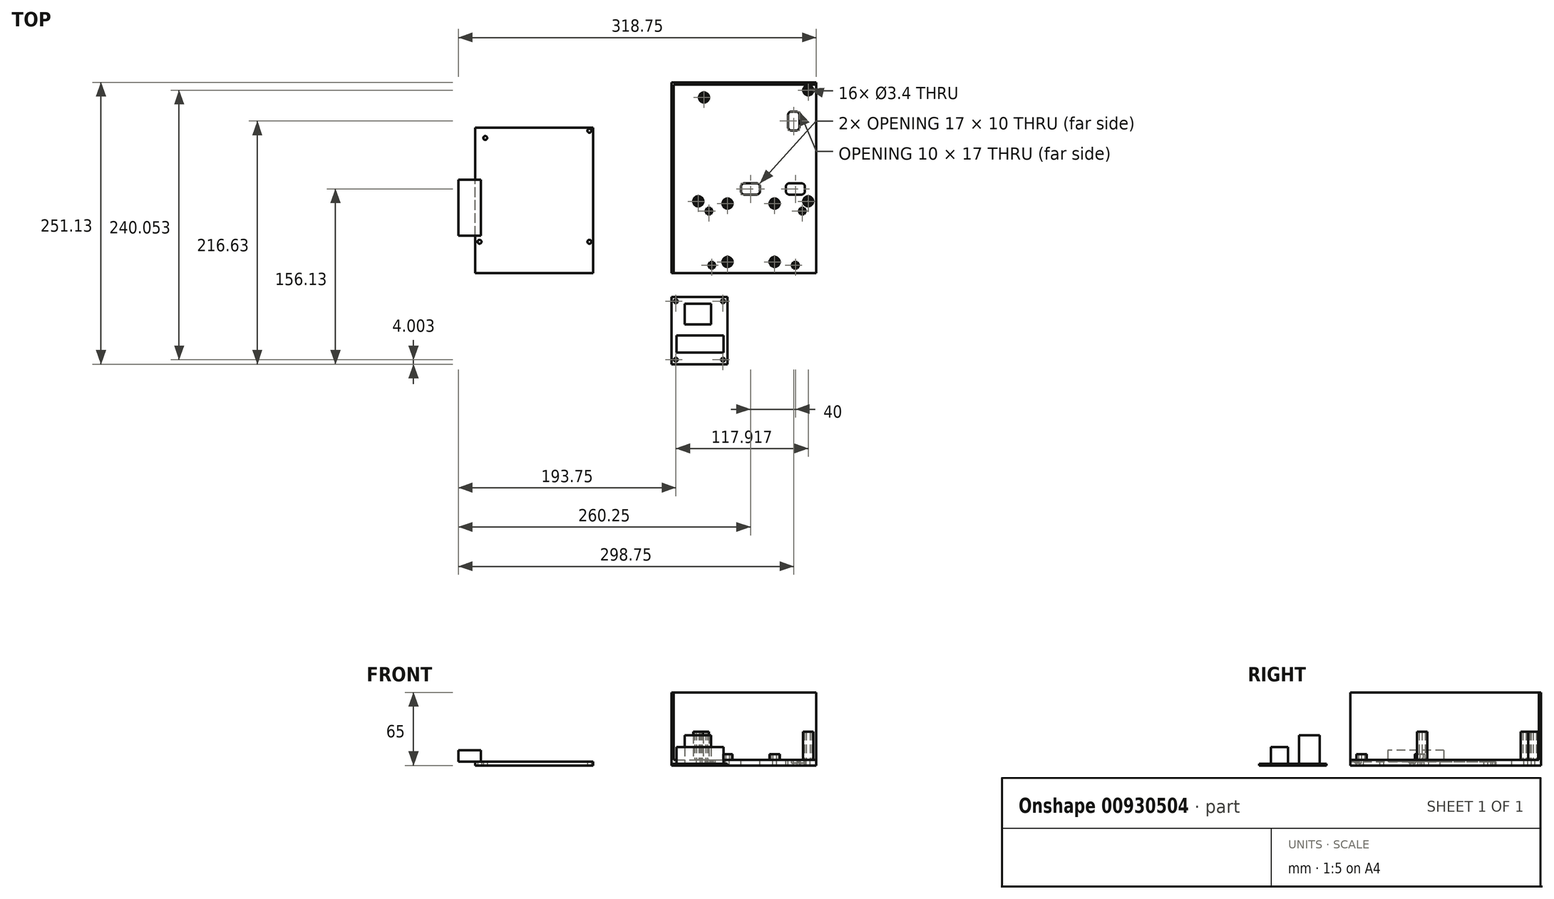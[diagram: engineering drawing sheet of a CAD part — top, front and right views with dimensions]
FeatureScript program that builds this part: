
annotation { "Feature Type Name" : "Feature", "Feature Type Description" : "" }
export const myFeature = defineFeature(function(context is Context, id is Id, definition is map)
    precondition{}
    {
        {
            assignVariable(context, id + "F0", {"variableType" : VariableType.LENGTH, "name" : "M3HoleDiameter", "lengthValue" : 3.4 * mm});
        }
        {
            assignVariable(context, id + "F1", {"variableType" : VariableType.LENGTH, "name" : "M3HexNutDepth", "lengthValue" : 2.8 * mm});
        }
        {
            var Q0;
            Q0=qCreatedBy(makeId("Top.planeOp"),FACE);
            var sketch = newSketch(context, id + "F2", { "sketchPlane" : qUnion([Q0])});
            skLineSegment(sketch, "E0.bottom", {"start": v(-174.75, 0) * mm, "end": v(-69.71, 0) * mm});
            skLineSegment(sketch, "E0.top", {"start": v(-174.75, 129.57) * mm, "end": v(-69.71, 129.57) * mm});
            skLineSegment(sketch, "E0.left", {"start": v(-174.75, 0) * mm, "end": v(-174.75, 129.57) * mm});
            skLineSegment(sketch, "E0.right", {"start": v(-69.71, 0) * mm, "end": v(-69.71, 129.57) * mm});
            skPoint(sketch, "E1", {"position": v(-170.94, 27.96) * mm});
            skPoint(sketch, "E2", {"position": v(-73.03, 27.96) * mm});
            skPoint(sketch, "E3", {"position": v(-73.03, 126.88) * mm});
            skPoint(sketch, "E4", {"position": v(-165.86, 120.41) * mm});
            skCircle(sketch, "E5", {"center": v(-165.86, 120.41) * mm, "radius": 1.75 * mm});
            skCircle(sketch, "E6", {"center": v(-73.03, 126.88) * mm, "radius": 1.75 * mm});
            skCircle(sketch, "E7", {"center": v(-170.94, 27.96) * mm, "radius": 1.75 * mm});
            skCircle(sketch, "E8", {"center": v(-73.03, 27.96) * mm, "radius": 1.75 * mm});
            skSolve(sketch);
        }
        {
            var Q0;
            Q0 = qSketchRegion(id + "F2", true);
            extrude(context, id + "F3", {"entities" : qUnion([Q0]), "depth" : 3.5 * mm, "offsetDistance" : 25 * mm});
        }
        {
            var Q0;
            Q0=makeQuery(id+"F3.opExtrude","CAP_FACE",FACE,{"disambiguationData":[OSD([sQuery(id+"F2.wireOp",EDGE,"E0.bottom"),sQuery(id+"F2.wireOp",EDGE,"E0.top"),sQuery(id+"F2.wireOp",EDGE,"E0.left"),sQuery(id+"F2.wireOp",EDGE,"E0.right"),sQuery(id+"F2.wireOp",EDGE,"E5"),sQuery(id+"F2.wireOp",EDGE,"E6"),sQuery(id+"F2.wireOp",EDGE,"E7"),sQuery(id+"F2.wireOp",EDGE,"E8")])],"isStart":false});
            var sketch = newSketch(context, id + "F4", { "sketchPlane" : qUnion([Q0])});
            skLineSegment(sketch, "E9.bottom", {"start": v(-174.75, 33.29) * mm, "end": v(-189.75, 33.29) * mm});
            skLineSegment(sketch, "E9.top", {"start": v(-174.75, 83.29) * mm, "end": v(-189.75, 83.29) * mm});
            skLineSegment(sketch, "E9.left", {"start": v(-174.75, 33.29) * mm, "end": v(-174.75, 83.29) * mm});
            skLineSegment(sketch, "E9.right", {"start": v(-189.75, 33.29) * mm, "end": v(-189.75, 83.29) * mm});
            skLineSegment(sketch, "E10.bottom", {"start": v(-174.75, 83.29) * mm, "end": v(-169.75, 83.29) * mm});
            skLineSegment(sketch, "E10.top", {"start": v(-174.75, 33.29) * mm, "end": v(-169.75, 33.29) * mm});
            skLineSegment(sketch, "E10.left", {"start": v(-174.75, 83.29) * mm, "end": v(-174.75, 33.29) * mm});
            skLineSegment(sketch, "E10.right", {"start": v(-169.75, 83.29) * mm, "end": v(-169.75, 33.29) * mm});
            skSolve(sketch);
        }
        {
            var Q0;
            Q0 = qSketchRegion(id + "F4", true);
            extrude(context, id + "F5", {"entities" : qUnion([Q0]), "operationType" : NewBodyOperationType.ADD, "depth" : 10 * mm, "offsetDistance" : 25 * mm});
        }
        {
            var Q0;
            Q0=qCreatedBy(makeId("Top.planeOp"),FACE);
            var sketch = newSketch(context, id + "F6", { "sketchPlane" : qUnion([Q0])});
            skLineSegment(sketch, "E11.bottom", {"start": v(0, -81.13) * mm, "end": v(50, -81.13) * mm});
            skLineSegment(sketch, "E11.top", {"start": v(0, -21.13) * mm, "end": v(50, -21.13) * mm});
            skLineSegment(sketch, "E11.left", {"start": v(0, -81.13) * mm, "end": v(0, -21.13) * mm});
            skLineSegment(sketch, "E11.right", {"start": v(50, -81.13) * mm, "end": v(50, -21.13) * mm});
            skPoint(sketch, "E12", {"position": v(4, -25.13) * mm});
            skPoint(sketch, "E13", {"position": v(46, -25.13) * mm});
            skPoint(sketch, "E14", {"position": v(4, -77.13) * mm});
            skPoint(sketch, "E15", {"position": v(46, -77.13) * mm});
            skCircle(sketch, "E16", {"center": v(4, -25.13) * mm, "radius": 1.7 * mm});
            skCircle(sketch, "E17", {"center": v(46, -25.13) * mm, "radius": 1.7 * mm});
            skCircle(sketch, "E18", {"center": v(4, -77.13) * mm, "radius": 1.7 * mm});
            skCircle(sketch, "E19", {"center": v(46, -77.13) * mm, "radius": 1.7 * mm});
            skSolve(sketch);
        }
        {
            var Q0;
            Q0 = qSketchRegion(id + "F6", true);
            extrude(context, id + "F7", {"entities" : qUnion([Q0]), "depth" : 1.5 * mm, "offsetDistance" : 25 * mm});
        }
        {
            var Q0;
            Q0=makeQuery(id+"F7.opExtrude","CAP_FACE",FACE,{"disambiguationData":[OSD([sQuery(id+"F6.wireOp",EDGE,"E11.bottom"),sQuery(id+"F6.wireOp",EDGE,"E11.top"),sQuery(id+"F6.wireOp",EDGE,"E11.left"),sQuery(id+"F6.wireOp",EDGE,"E11.right"),sQuery(id+"F6.wireOp",EDGE,"E16"),sQuery(id+"F6.wireOp",EDGE,"E17"),sQuery(id+"F6.wireOp",EDGE,"E18"),sQuery(id+"F6.wireOp",EDGE,"E19")])],"isStart":false});
            var sketch = newSketch(context, id + "F8", { "sketchPlane" : qUnion([Q0])});
            skLineSegment(sketch, "E20.bottom", {"start": v(4.5, -70.63) * mm, "end": v(46.5, -70.63) * mm});
            skLineSegment(sketch, "E20.top", {"start": v(4.5, -55.63) * mm, "end": v(46.5, -55.63) * mm});
            skLineSegment(sketch, "E20.left", {"start": v(4.5, -70.63) * mm, "end": v(4.5, -55.63) * mm});
            skLineSegment(sketch, "E20.right", {"start": v(46.5, -70.63) * mm, "end": v(46.5, -55.63) * mm});
            skSolve(sketch);
        }
        {
            var Q0;
            Q0 = qSketchRegion(id + "F8", true);
            extrude(context, id + "F9", {"entities" : qUnion([Q0]), "operationType" : NewBodyOperationType.ADD, "depth" : 15 * mm, "offsetDistance" : 25 * mm});
        }
        {
            var Q0;
            Q0=makeQuery(id+"F7.opExtrude","CAP_FACE",FACE,{"disambiguationData":[OSD([sQuery(id+"F6.wireOp",EDGE,"E11.bottom"),sQuery(id+"F6.wireOp",EDGE,"E11.top"),sQuery(id+"F6.wireOp",EDGE,"E11.left"),sQuery(id+"F6.wireOp",EDGE,"E11.right"),sQuery(id+"F6.wireOp",EDGE,"E16"),sQuery(id+"F6.wireOp",EDGE,"E17"),sQuery(id+"F6.wireOp",EDGE,"E18"),sQuery(id+"F6.wireOp",EDGE,"E19")])],"isStart":false});
            var sketch = newSketch(context, id + "F10", { "sketchPlane" : qUnion([Q0])});
            skLineSegment(sketch, "E21.bottom", {"start": v(11.75, -27.13) * mm, "end": v(35.25, -27.13) * mm});
            skLineSegment(sketch, "E21.top", {"start": v(11.75, -45.63) * mm, "end": v(35.25, -45.63) * mm});
            skLineSegment(sketch, "E21.left", {"start": v(11.75, -27.13) * mm, "end": v(11.75, -45.63) * mm});
            skLineSegment(sketch, "E21.right", {"start": v(35.25, -27.13) * mm, "end": v(35.25, -45.63) * mm});
            skSolve(sketch);
        }
        {
            var Q0;
            Q0 = qSketchRegion(id + "F10", true);
            extrude(context, id + "F11", {"entities" : qUnion([Q0]), "operationType" : NewBodyOperationType.ADD, "depth" : 25.5 * mm, "offsetDistance" : 25 * mm});
        }
        {
            var Q0;
            Q0=qCreatedBy(makeId("Top.planeOp"),FACE);
            var sketch = newSketch(context, id + "F12", { "sketchPlane" : qUnion([Q0])});
            skLineSegment(sketch, "E22.bottom", {"start": v(0, 0) * mm, "end": v(129, 0) * mm});
            skLineSegment(sketch, "E22.top", {"start": v(0, 170) * mm, "end": v(129, 170) * mm});
            skLineSegment(sketch, "E22.left", {"start": v(0, 0) * mm, "end": v(0, 170) * mm});
            skLineSegment(sketch, "E22.right", {"start": v(129, 0) * mm, "end": v(129, 170) * mm});
            skSolve(sketch);
        }
        {
            var Q0;
            Q0 = qSketchRegion(id + "F12", true);
            extrude(context, id + "F13", {"entities" : qUnion([Q0]), "depth" : 5 * mm, "offsetDistance" : 25 * mm});
        }
        {
            var Q0;
            Q0=makeQuery(id+"F13.opExtrude","CAP_FACE",FACE,{"disambiguationData":[OSD([sQuery(id+"F12.wireOp",EDGE,"E22.bottom"),sQuery(id+"F12.wireOp",EDGE,"E22.top"),sQuery(id+"F12.wireOp",EDGE,"E22.left"),sQuery(id+"F12.wireOp",EDGE,"E22.right"),sQuery(id+"F12.wireOp",EDGE,"ENlJJPwH-t7wi-Tg4m-EIBb-eTt2GZQg3k3P.top"),sQuery(id+"F12.wireOp",EDGE,"ENlJJPwH-t7wi-Tg4m-EIBb-eTt2GZQg3k3P.left"),sQuery(id+"F12.wireOp",EDGE,"ENlJJPwH-t7wi-Tg4m-EIBb-eTt2GZQg3k3P.right"),sQuery(id+"F12.wireOp",EDGE,"590sdj5N-QSTJ-qvK5-s69I-Y719Xk4BLkaZ.top"),sQuery(id+"F12.wireOp",EDGE,"590sdj5N-QSTJ-qvK5-s69I-Y719Xk4BLkaZ.left"),sQuery(id+"F12.wireOp",EDGE,"590sdj5N-QSTJ-qvK5-s69I-Y719Xk4BLkaZ.right"),sQuery(id+"F12.wireOp",EDGE,"boF4sXyi-6WZN-pan6-Kfs4-asuBxe9Vqafz.top"),sQuery(id+"F12.wireOp",EDGE,"boF4sXyi-6WZN-pan6-Kfs4-asuBxe9Vqafz.left"),sQuery(id+"F12.wireOp",EDGE,"boF4sXyi-6WZN-pan6-Kfs4-asuBxe9Vqafz.right"),sQuery(id+"F12.wireOp",EDGE,"VC2s6hMx-ooNF-aeXA-kSyT-K1uUBSIoU8fE.top"),sQuery(id+"F12.wireOp",EDGE,"VC2s6hMx-ooNF-aeXA-kSyT-K1uUBSIoU8fE.left"),sQuery(id+"F12.wireOp",EDGE,"VC2s6hMx-ooNF-aeXA-kSyT-K1uUBSIoU8fE.right")])],"isStart":false});
            var sketch = newSketch(context, id + "F14", { "sketchPlane" : qUnion([Q0])});
            skPoint(sketch, "E23", {"position": v(36, 7) * mm});
            skPoint(sketch, "E24", {"position": v(110.5, 7) * mm});
            skPoint(sketch, "E25", {"position": v(33.5, 55.2) * mm});
            skPoint(sketch, "E26", {"position": v(116.7, 55.2) * mm});
            skCircle(sketch, "E27.cCircle", {"center": v(33.5, 55.2) * mm, "radius": 2.8 * mm, "construction": true});
            skLineSegment(sketch, "E27.0", {"start": v(31.88, 58) * mm, "end": v(35.12, 58) * mm});
            skLineSegment(sketch, "E27.1", {"start": v(35.12, 58) * mm, "end": v(36.73, 55.2) * mm});
            skLineSegment(sketch, "E27.2", {"start": v(36.73, 55.2) * mm, "end": v(35.12, 52.4) * mm});
            skLineSegment(sketch, "E27.3", {"start": v(35.12, 52.4) * mm, "end": v(31.88, 52.4) * mm});
            skLineSegment(sketch, "E27.4", {"start": v(31.88, 52.4) * mm, "end": v(30.27, 55.2) * mm});
            skLineSegment(sketch, "E27.5", {"start": v(30.27, 55.2) * mm, "end": v(31.88, 58) * mm});
            skPoint(sketch, "E27.0.midPoint", {"position": v(33.5, 58) * mm});
            skCircle(sketch, "E28.cCircle", {"center": v(116.7, 55.2) * mm, "radius": 2.8 * mm, "construction": true});
            skLineSegment(sketch, "E28.0", {"start": v(115.08, 58) * mm, "end": v(118.32, 58) * mm});
            skLineSegment(sketch, "E28.1", {"start": v(118.32, 58) * mm, "end": v(119.93, 55.2) * mm});
            skLineSegment(sketch, "E28.2", {"start": v(119.93, 55.2) * mm, "end": v(118.32, 52.4) * mm});
            skLineSegment(sketch, "E28.3", {"start": v(118.32, 52.4) * mm, "end": v(115.08, 52.4) * mm});
            skLineSegment(sketch, "E28.4", {"start": v(115.08, 52.4) * mm, "end": v(113.47, 55.2) * mm});
            skLineSegment(sketch, "E28.5", {"start": v(113.47, 55.2) * mm, "end": v(115.08, 58) * mm});
            skPoint(sketch, "E28.0.midPoint", {"position": v(116.7, 58) * mm});
            skCircle(sketch, "E29.cCircle", {"center": v(110.5, 7) * mm, "radius": 2.8 * mm, "construction": true});
            skLineSegment(sketch, "E29.0", {"start": v(108.88, 9.8) * mm, "end": v(112.12, 9.8) * mm});
            skLineSegment(sketch, "E29.1", {"start": v(112.12, 9.8) * mm, "end": v(113.73, 7) * mm});
            skLineSegment(sketch, "E29.2", {"start": v(113.73, 7) * mm, "end": v(112.12, 4.2) * mm});
            skLineSegment(sketch, "E29.3", {"start": v(112.12, 4.2) * mm, "end": v(108.88, 4.2) * mm});
            skLineSegment(sketch, "E29.4", {"start": v(108.88, 4.2) * mm, "end": v(107.27, 7) * mm});
            skLineSegment(sketch, "E29.5", {"start": v(107.27, 7) * mm, "end": v(108.88, 9.8) * mm});
            skPoint(sketch, "E29.0.midPoint", {"position": v(110.5, 9.8) * mm});
            skCircle(sketch, "E30.cCircle", {"center": v(36, 7) * mm, "radius": 2.8 * mm, "construction": true});
            skLineSegment(sketch, "E30.0", {"start": v(34.38, 9.8) * mm, "end": v(37.62, 9.8) * mm});
            skLineSegment(sketch, "E30.1", {"start": v(37.62, 9.8) * mm, "end": v(39.23, 7) * mm});
            skLineSegment(sketch, "E30.2", {"start": v(39.23, 7) * mm, "end": v(37.62, 4.2) * mm});
            skLineSegment(sketch, "E30.3", {"start": v(37.62, 4.2) * mm, "end": v(34.38, 4.2) * mm});
            skLineSegment(sketch, "E30.4", {"start": v(34.38, 4.2) * mm, "end": v(32.77, 7) * mm});
            skLineSegment(sketch, "E30.5", {"start": v(32.77, 7) * mm, "end": v(34.38, 9.8) * mm});
            skPoint(sketch, "E30.0.midPoint", {"position": v(36, 9.8) * mm});
            skSolve(sketch);
        }
        {
            var Q0;
            Q0=sQuery(id+"F14.wireOp",VERTEX,"E25");
            var Q1;
            Q1=sQuery(id+"F14.wireOp",VERTEX,"E28.cCircle.center");
            var Q2;
            Q2=sQuery(id+"F14.wireOp",VERTEX,"E29.cCircle.center");
            var Q3;
            Q3=sQuery(id+"F14.wireOp",VERTEX,"E30.cCircle.center");
            var Q4;
            Q4=sQuery(id+"F14.wireOp",VERTEX,"66780121-3f7c-4df2-9e8e-298b6627a8a1.cCircle.center");
            var Q5;
            Q5=sQuery(id+"F14.wireOp",VERTEX,"7a8d0383-0dc8-4305-b331-709482cf3036");
            var Q6;
            Q6=sQuery(id+"F14.wireOp",VERTEX,"6d33d0c3-34ed-4e35-861e-9c01af61f537");
            var Q7;
            Q7=sQuery(id+"F14.wireOp",VERTEX,"b813c6d9-d0bb-4b40-90eb-9f39a377eb20.cCircle.center");
            var Q8;
            Q8=sQuery(id+"F14.wireOp",VERTEX,"7464b1d7-4f39-41f7-8282-fd3c08e524e5");
            var Q9;
            Q9=sQuery(id+"F14.wireOp",VERTEX,"ce837585-52f0-452e-9ccc-18a1bac3b544");
            var Q10;
            Q10=makeQuery(id+"F13.opExtrude","SWEPT_BODY",BODY,{"disambiguationData":[OSD([sQuery(id+"F12.wireOp",EDGE,"E22.bottom"),sQuery(id+"F12.wireOp",EDGE,"E22.top"),sQuery(id+"F12.wireOp",EDGE,"E22.left"),sQuery(id+"F12.wireOp",EDGE,"E22.right"),sQuery(id+"F12.wireOp",EDGE,"ENlJJPwH-t7wi-Tg4m-EIBb-eTt2GZQg3k3P.top"),sQuery(id+"F12.wireOp",EDGE,"ENlJJPwH-t7wi-Tg4m-EIBb-eTt2GZQg3k3P.left"),sQuery(id+"F12.wireOp",EDGE,"ENlJJPwH-t7wi-Tg4m-EIBb-eTt2GZQg3k3P.right"),sQuery(id+"F12.wireOp",EDGE,"590sdj5N-QSTJ-qvK5-s69I-Y719Xk4BLkaZ.top"),sQuery(id+"F12.wireOp",EDGE,"590sdj5N-QSTJ-qvK5-s69I-Y719Xk4BLkaZ.left"),sQuery(id+"F12.wireOp",EDGE,"590sdj5N-QSTJ-qvK5-s69I-Y719Xk4BLkaZ.right"),sQuery(id+"F12.wireOp",EDGE,"boF4sXyi-6WZN-pan6-Kfs4-asuBxe9Vqafz.top"),sQuery(id+"F12.wireOp",EDGE,"boF4sXyi-6WZN-pan6-Kfs4-asuBxe9Vqafz.left"),sQuery(id+"F12.wireOp",EDGE,"boF4sXyi-6WZN-pan6-Kfs4-asuBxe9Vqafz.right"),sQuery(id+"F12.wireOp",EDGE,"VC2s6hMx-ooNF-aeXA-kSyT-K1uUBSIoU8fE.top"),sQuery(id+"F12.wireOp",EDGE,"VC2s6hMx-ooNF-aeXA-kSyT-K1uUBSIoU8fE.left"),sQuery(id+"F12.wireOp",EDGE,"VC2s6hMx-ooNF-aeXA-kSyT-K1uUBSIoU8fE.right")])]});
            hole(context, id + "F15", {"style" : HoleStyle.SIMPLE, "endStyle" : HoleEndStyle.THROUGH, "holeDiameter" : getVariable(context, 'M3HoleDiameter'), "majorDiameter" : 5 * mm, "isTappedThrough" : true, "tappedDepth" : 12 * mm, "tapClearance" : 3, "locations" : qUnion([Q0, Q1, Q2, Q3, Q4, Q5, Q6, Q7, Q8, Q9]), "scope" : qUnion([Q10])});
        }
        {
            var Q0;
            Q0 = qSketchRegion(id + "F14", true);
            extrude(context, id + "F16", {"entities" : qUnion([Q0]), "operationType" : NewBodyOperationType.REMOVE, "oppositeDirection" : true, "depth" : getVariable(context, 'M3HexNutDepth'), "offsetDistance" : 25 * mm});
        }
        {
            var Q0;
            {var subQ0=sQuery(id+"F12.wireOp",EDGE,"VC2s6hMx-ooNF-aeXA-kSyT-K1uUBSIoU8fE.right");var subQ1=sQuery(id+"F12.wireOp",EDGE,"VC2s6hMx-ooNF-aeXA-kSyT-K1uUBSIoU8fE.top");var subQ2=sQuery(id+"F12.wireOp",EDGE,"boF4sXyi-6WZN-pan6-Kfs4-asuBxe9Vqafz.left");var subQ3=sQuery(id+"F12.wireOp",EDGE,"ENlJJPwH-t7wi-Tg4m-EIBb-eTt2GZQg3k3P.left");var subQ4=sQuery(id+"F12.wireOp",EDGE,"E22.left");var subQ5=sQuery(id+"F12.wireOp",EDGE,"E22.top");var subQ6=sQuery(id+"F12.wireOp",EDGE,"VC2s6hMx-ooNF-aeXA-kSyT-K1uUBSIoU8fE.left");var subQ7=sQuery(id+"F12.wireOp",EDGE,"590sdj5N-QSTJ-qvK5-s69I-Y719Xk4BLkaZ.left");var subQ8=sQuery(id+"F12.wireOp",EDGE,"E22.right");var subQ9=sQuery(id+"F12.wireOp",EDGE,"E22.bottom");var subQ10=sQuery(id+"F12.wireOp",EDGE,"boF4sXyi-6WZN-pan6-Kfs4-asuBxe9Vqafz.right");var subQ11=sQuery(id+"F12.wireOp",EDGE,"ENlJJPwH-t7wi-Tg4m-EIBb-eTt2GZQg3k3P.top");var subQ12=sQuery(id+"F12.wireOp",EDGE,"ENlJJPwH-t7wi-Tg4m-EIBb-eTt2GZQg3k3P.right");var subQ13=sQuery(id+"F12.wireOp",EDGE,"590sdj5N-QSTJ-qvK5-s69I-Y719Xk4BLkaZ.top");var subQ14=sQuery(id+"F12.wireOp",EDGE,"590sdj5N-QSTJ-qvK5-s69I-Y719Xk4BLkaZ.right");var subQ15=sQuery(id+"F12.wireOp",EDGE,"boF4sXyi-6WZN-pan6-Kfs4-asuBxe9Vqafz.top");Q0=makeQuery(id+"FK80XC3gcnQsNLE_2.boolean.opBoolean","SPLIT",FACE,{"disambiguationData":[TD([makeQuery(id+"F13.opExtrude","SWEPT_FACE",FACE,{"disambiguationData":[OSD([subQ9])]})])],"derivedFrom":makeQuery(id+"F13.opExtrude","CAP_FACE",FACE,{"disambiguationData":[OSD([subQ9,subQ5,subQ4,subQ8,subQ11,subQ3,subQ12,subQ13,subQ7,subQ14,subQ15,subQ2,subQ10,subQ1,subQ6,subQ0])],"isStart":false})});}
            var sketch = newSketch(context, id + "F17", { "sketchPlane" : qUnion([Q0])});
            skPoint(sketch, "E31", {"position": v(24, 64) * mm});
            skPoint(sketch, "E32", {"position": v(121.92, 64) * mm});
            skPoint(sketch, "E33", {"position": v(29.08, 156.46) * mm});
            skPoint(sketch, "E34", {"position": v(121.92, 162.93) * mm});
            skCircle(sketch, "E35", {"center": v(29.08, 156.46) * mm, "radius": 1.7 * mm});
            skCircle(sketch, "E36", {"center": v(29.08, 156.46) * mm, "radius": 4.5 * mm});
            skCircle(sketch, "E37", {"center": v(121.92, 162.93) * mm, "radius": 1.7 * mm});
            skCircle(sketch, "E38", {"center": v(121.92, 162.93) * mm, "radius": 4.5 * mm});
            skCircle(sketch, "E39", {"center": v(24, 64) * mm, "radius": 1.7 * mm});
            skCircle(sketch, "E40", {"center": v(24, 64) * mm, "radius": 4.5 * mm});
            skCircle(sketch, "E41", {"center": v(121.92, 64) * mm, "radius": 1.7 * mm});
            skCircle(sketch, "E42", {"center": v(121.92, 64) * mm, "radius": 4.5 * mm});
            skCircle(sketch, "E43.cCircle", {"center": v(29.08, 156.46) * mm, "radius": 2.8 * mm, "construction": true});
            skLineSegment(sketch, "E43.0", {"start": v(27.46, 159.26) * mm, "end": v(30.7, 159.26) * mm});
            skLineSegment(sketch, "E43.1", {"start": v(30.7, 159.26) * mm, "end": v(32.31, 156.46) * mm});
            skLineSegment(sketch, "E43.2", {"start": v(32.31, 156.46) * mm, "end": v(30.7, 153.66) * mm});
            skLineSegment(sketch, "E43.3", {"start": v(30.7, 153.66) * mm, "end": v(27.46, 153.66) * mm});
            skLineSegment(sketch, "E43.4", {"start": v(27.46, 153.66) * mm, "end": v(25.85, 156.46) * mm});
            skLineSegment(sketch, "E43.5", {"start": v(25.85, 156.46) * mm, "end": v(27.46, 159.26) * mm});
            skPoint(sketch, "E43.0.midPoint", {"position": v(29.08, 159.26) * mm});
            skCircle(sketch, "E44.cCircle", {"center": v(121.92, 162.93) * mm, "radius": 2.8 * mm, "construction": true});
            skLineSegment(sketch, "E44.0", {"start": v(120.3, 165.73) * mm, "end": v(123.53, 165.73) * mm});
            skLineSegment(sketch, "E44.1", {"start": v(123.53, 165.73) * mm, "end": v(125.15, 162.93) * mm});
            skLineSegment(sketch, "E44.2", {"start": v(125.15, 162.93) * mm, "end": v(123.53, 160.13) * mm});
            skLineSegment(sketch, "E44.3", {"start": v(123.53, 160.13) * mm, "end": v(120.3, 160.13) * mm});
            skLineSegment(sketch, "E44.4", {"start": v(120.3, 160.13) * mm, "end": v(118.68, 162.93) * mm});
            skLineSegment(sketch, "E44.5", {"start": v(118.68, 162.93) * mm, "end": v(120.3, 165.73) * mm});
            skPoint(sketch, "E44.0.midPoint", {"position": v(121.92, 165.73) * mm});
            skCircle(sketch, "E45.cCircle", {"center": v(24, 64) * mm, "radius": 2.8 * mm, "construction": true});
            skLineSegment(sketch, "E45.0", {"start": v(22.38, 66.8) * mm, "end": v(25.62, 66.8) * mm});
            skLineSegment(sketch, "E45.1", {"start": v(25.62, 66.8) * mm, "end": v(27.23, 64) * mm});
            skLineSegment(sketch, "E45.2", {"start": v(27.23, 64) * mm, "end": v(25.62, 61.2) * mm});
            skLineSegment(sketch, "E45.3", {"start": v(25.62, 61.2) * mm, "end": v(22.38, 61.2) * mm});
            skLineSegment(sketch, "E45.4", {"start": v(22.38, 61.2) * mm, "end": v(20.77, 64) * mm});
            skLineSegment(sketch, "E45.5", {"start": v(20.77, 64) * mm, "end": v(22.38, 66.8) * mm});
            skPoint(sketch, "E45.0.midPoint", {"position": v(24, 66.8) * mm});
            skCircle(sketch, "E46.cCircle", {"center": v(121.92, 64) * mm, "radius": 2.8 * mm, "construction": true});
            skLineSegment(sketch, "E46.0", {"start": v(120.3, 66.8) * mm, "end": v(123.53, 66.8) * mm});
            skLineSegment(sketch, "E46.1", {"start": v(123.53, 66.8) * mm, "end": v(125.15, 64) * mm});
            skLineSegment(sketch, "E46.2", {"start": v(125.15, 64) * mm, "end": v(123.53, 61.2) * mm});
            skLineSegment(sketch, "E46.3", {"start": v(123.53, 61.2) * mm, "end": v(120.3, 61.2) * mm});
            skLineSegment(sketch, "E46.4", {"start": v(120.3, 61.2) * mm, "end": v(118.68, 64) * mm});
            skLineSegment(sketch, "E46.5", {"start": v(118.68, 64) * mm, "end": v(120.3, 66.8) * mm});
            skPoint(sketch, "E46.0.midPoint", {"position": v(121.92, 66.8) * mm});
            skSolve(sketch);
        }
        {
            var Q0;
            Q0=sQuery(id+"F17.wireOp",VERTEX,"E33");
            var Q1;
            Q1=sQuery(id+"F17.wireOp",VERTEX,"E34");
            var Q2;
            Q2=sQuery(id+"F17.wireOp",VERTEX,"E32");
            var Q3;
            Q3=sQuery(id+"F17.wireOp",VERTEX,"E39.center");
            var Q4;
            Q4=makeQuery(id+"F13.opExtrude","SWEPT_BODY",BODY,{"disambiguationData":[OSD([sQuery(id+"F12.wireOp",EDGE,"E22.bottom"),sQuery(id+"F12.wireOp",EDGE,"E22.top"),sQuery(id+"F12.wireOp",EDGE,"E22.left"),sQuery(id+"F12.wireOp",EDGE,"E22.right")])]});
            hole(context, id + "F18", {"style" : HoleStyle.SIMPLE, "endStyle" : HoleEndStyle.THROUGH, "holeDiameter" : getVariable(context, 'M3HoleDiameter'), "majorDiameter" : 5 * mm, "isTappedThrough" : true, "tappedDepth" : 12 * mm, "tapClearance" : 3, "locations" : qUnion([Q0, Q1, Q2, Q3]), "scope" : qUnion([Q4])});
        }
        {
            var Q0;
            Q0 = qSketchRegion(id + "F17", true);
            extrude(context, id + "F19", {"entities" : qUnion([Q0]), "operationType" : NewBodyOperationType.ADD, "depth" : 25 * mm, "offsetDistance" : 25 * mm});
        }
        {
            var Q0;
            Q0=makeQuery(id+"F17.imprint","IMPRINT",FACE,{"disambiguationData":[TD([[makeQuery(id+"F17.imprint","IMPRINT",EDGE,{"derivedFrom":sQuery(id+"F17.wireOp",EDGE,"E36")}),-1.0]])]});
            var sketch = newSketch(context, id + "F20", { "sketchPlane" : qUnion([Q0])});
            skLineSegment(sketch, "E47", {"start": v(0, 0) * mm, "end": v(0, 170) * mm});
            skLineSegment(sketch, "E48", {"start": v(0, 170) * mm, "end": v(129, 170) * mm});
            skLineSegment(sketch, "E49", {"start": v(129, 170) * mm, "end": v(129, 168) * mm});
            skLineSegment(sketch, "E50", {"start": v(129, 168) * mm, "end": v(2, 168) * mm});
            skLineSegment(sketch, "E51", {"start": v(2, 168) * mm, "end": v(2, 0) * mm});
            skLineSegment(sketch, "E52", {"start": v(2, 0) * mm, "end": v(0, 0) * mm});
            skSolve(sketch);
        }
        {
            var Q0;
            Q0 = qSketchRegion(id + "F20", true);
            extrude(context, id + "F21", {"entities" : qUnion([Q0]), "operationType" : NewBodyOperationType.ADD, "depth" : 60 * mm, "offsetDistance" : 25 * mm});
        }
        {
            var Q0;
            Q0=makeQuery(id+"F17.imprint","IMPRINT",FACE,{"disambiguationData":[TD([[makeQuery(id+"F17.imprint","IMPRINT",EDGE,{"derivedFrom":sQuery(id+"F17.wireOp",EDGE,"E36")}),-1.0]])]});
            var sketch = newSketch(context, id + "F22", { "sketchPlane" : qUnion([Q0])});
            skPoint(sketch, "E53", {"position": v(50, 10) * mm});
            skPoint(sketch, "E54", {"position": v(92, 10) * mm});
            skPoint(sketch, "E55", {"position": v(50, 62) * mm});
            skPoint(sketch, "E56", {"position": v(92, 62) * mm});
            skCircle(sketch, "E57", {"center": v(50, 10) * mm, "radius": 1.7 * mm});
            skCircle(sketch, "E58", {"center": v(50, 10) * mm, "radius": 4.5 * mm});
            skCircle(sketch, "E59", {"center": v(92, 10) * mm, "radius": 1.7 * mm});
            skCircle(sketch, "E60", {"center": v(92, 10) * mm, "radius": 4.5 * mm});
            skCircle(sketch, "E61", {"center": v(50, 62) * mm, "radius": 1.7 * mm});
            skCircle(sketch, "E62", {"center": v(50, 62) * mm, "radius": 4.5 * mm});
            skCircle(sketch, "E63", {"center": v(92, 62) * mm, "radius": 1.7 * mm});
            skCircle(sketch, "E64", {"center": v(92, 62) * mm, "radius": 4.5 * mm});
            skCircle(sketch, "E65.cCircle", {"center": v(50, 62) * mm, "radius": 2.8 * mm, "construction": true});
            skLineSegment(sketch, "E65.0", {"start": v(48.38, 64.8) * mm, "end": v(51.62, 64.8) * mm});
            skLineSegment(sketch, "E65.1", {"start": v(51.62, 64.8) * mm, "end": v(53.23, 62) * mm});
            skLineSegment(sketch, "E65.2", {"start": v(53.23, 62) * mm, "end": v(51.62, 59.2) * mm});
            skLineSegment(sketch, "E65.3", {"start": v(51.62, 59.2) * mm, "end": v(48.38, 59.2) * mm});
            skLineSegment(sketch, "E65.4", {"start": v(48.38, 59.2) * mm, "end": v(46.77, 62) * mm});
            skLineSegment(sketch, "E65.5", {"start": v(46.77, 62) * mm, "end": v(48.38, 64.8) * mm});
            skPoint(sketch, "E65.0.midPoint", {"position": v(50, 64.8) * mm});
            skCircle(sketch, "E66.cCircle", {"center": v(92, 62) * mm, "radius": 2.8 * mm, "construction": true});
            skLineSegment(sketch, "E66.0", {"start": v(90.38, 64.8) * mm, "end": v(93.62, 64.8) * mm});
            skLineSegment(sketch, "E66.1", {"start": v(93.62, 64.8) * mm, "end": v(95.23, 62) * mm});
            skLineSegment(sketch, "E66.2", {"start": v(95.23, 62) * mm, "end": v(93.62, 59.2) * mm});
            skLineSegment(sketch, "E66.3", {"start": v(93.62, 59.2) * mm, "end": v(90.38, 59.2) * mm});
            skLineSegment(sketch, "E66.4", {"start": v(90.38, 59.2) * mm, "end": v(88.77, 62) * mm});
            skLineSegment(sketch, "E66.5", {"start": v(88.77, 62) * mm, "end": v(90.38, 64.8) * mm});
            skPoint(sketch, "E66.0.midPoint", {"position": v(92, 64.8) * mm});
            skCircle(sketch, "E67.cCircle", {"center": v(50, 10) * mm, "radius": 2.8 * mm, "construction": true});
            skLineSegment(sketch, "E67.0", {"start": v(48.38, 12.8) * mm, "end": v(51.62, 12.8) * mm});
            skLineSegment(sketch, "E67.1", {"start": v(51.62, 12.8) * mm, "end": v(53.23, 10) * mm});
            skLineSegment(sketch, "E67.2", {"start": v(53.23, 10) * mm, "end": v(51.62, 7.2) * mm});
            skLineSegment(sketch, "E67.3", {"start": v(51.62, 7.2) * mm, "end": v(48.38, 7.2) * mm});
            skLineSegment(sketch, "E67.4", {"start": v(48.38, 7.2) * mm, "end": v(46.77, 10) * mm});
            skLineSegment(sketch, "E67.5", {"start": v(46.77, 10) * mm, "end": v(48.38, 12.8) * mm});
            skPoint(sketch, "E67.0.midPoint", {"position": v(50, 12.8) * mm});
            skCircle(sketch, "E68.cCircle", {"center": v(92, 10) * mm, "radius": 2.8 * mm, "construction": true});
            skLineSegment(sketch, "E68.0", {"start": v(90.38, 12.8) * mm, "end": v(93.62, 12.8) * mm});
            skLineSegment(sketch, "E68.1", {"start": v(93.62, 12.8) * mm, "end": v(95.23, 10) * mm});
            skLineSegment(sketch, "E68.2", {"start": v(95.23, 10) * mm, "end": v(93.62, 7.2) * mm});
            skLineSegment(sketch, "E68.3", {"start": v(93.62, 7.2) * mm, "end": v(90.38, 7.2) * mm});
            skLineSegment(sketch, "E68.4", {"start": v(90.38, 7.2) * mm, "end": v(88.77, 10) * mm});
            skLineSegment(sketch, "E68.5", {"start": v(88.77, 10) * mm, "end": v(90.38, 12.8) * mm});
            skPoint(sketch, "E68.0.midPoint", {"position": v(92, 12.8) * mm});
            skSolve(sketch);
        }
        {
            var Q0;
            Q0=sQuery(id+"F22.wireOp",VERTEX,"E55");
            var Q1;
            Q1=sQuery(id+"F22.wireOp",VERTEX,"E56");
            var Q2;
            Q2=sQuery(id+"F22.wireOp",VERTEX,"E54");
            var Q3;
            Q3=sQuery(id+"F22.wireOp",VERTEX,"E53");
            var Q4;
            Q4=makeQuery(id+"F13.opExtrude","SWEPT_BODY",BODY,{"disambiguationData":[OSD([sQuery(id+"F12.wireOp",EDGE,"E22.bottom"),sQuery(id+"F12.wireOp",EDGE,"E22.top"),sQuery(id+"F12.wireOp",EDGE,"E22.left"),sQuery(id+"F12.wireOp",EDGE,"E22.right")])]});
            hole(context, id + "F23", {"style" : HoleStyle.SIMPLE, "endStyle" : HoleEndStyle.THROUGH, "holeDiameter" : getVariable(context, 'M3HoleDiameter'), "majorDiameter" : 5 * mm, "isTappedThrough" : true, "tappedDepth" : 12 * mm, "tapClearance" : 3, "locations" : qUnion([Q0, Q1, Q2, Q3]), "scope" : qUnion([Q4])});
        }
        {
            var Q0;
            Q0 = qSketchRegion(id + "F22", true);
            extrude(context, id + "F24", {"entities" : qUnion([Q0]), "operationType" : NewBodyOperationType.ADD, "depth" : 5 * mm, "offsetDistance" : 25 * mm});
        }
        {
            var Q0;
            Q0=makeQuery(id+"F13.opExtrude","CAP_FACE",FACE,{"disambiguationData":[OSD([sQuery(id+"F12.wireOp",EDGE,"E22.bottom"),sQuery(id+"F12.wireOp",EDGE,"E22.top"),sQuery(id+"F12.wireOp",EDGE,"E22.left"),sQuery(id+"F12.wireOp",EDGE,"E22.right")])],"isStart":false});
            var sketch = newSketch(context, id + "F25", { "sketchPlane" : qUnion([Q0])});
            skPoint(sketch, "E69", {"position": v(62, 70) * mm});
            skPoint(sketch, "E70", {"position": v(62, 80) * mm});
            skLineSegment(sketch, "E71.bottom", {"start": v(65, 70) * mm, "end": v(76, 70) * mm});
            skLineSegment(sketch, "E71.top", {"start": v(65, 80) * mm, "end": v(76, 80) * mm});
            skLineSegment(sketch, "E71.left", {"start": v(62, 73) * mm, "end": v(62, 77) * mm});
            skLineSegment(sketch, "E71.right", {"start": v(79, 73) * mm, "end": v(79, 77) * mm});
            skPoint(sketch, "E72.visualSharp", {"position": v(79, 80) * mm});
            skArc(sketch, "E72.filletArc", {"start": v(79, 77) * mm, "mid": v(78.12, 79.12) * mm, "end": v(76, 80) * mm});
            skPoint(sketch, "E73.visualSharp", {"position": v(79, 70) * mm});
            skArc(sketch, "E73.filletArc", {"start": v(76, 70) * mm, "mid": v(78.12, 70.88) * mm, "end": v(79, 73) * mm});
            skArc(sketch, "E74.filletArc", {"start": v(62, 73) * mm, "mid": v(62.88, 70.88) * mm, "end": v(65, 70) * mm});
            skArc(sketch, "E75.filletArc", {"start": v(65, 80) * mm, "mid": v(62.88, 79.12) * mm, "end": v(62, 77) * mm});
            skLineSegment(sketch, "E76.bottom", {"start": v(105, 80) * mm, "end": v(116, 80) * mm});
            skLineSegment(sketch, "E76.top", {"start": v(105, 70) * mm, "end": v(116, 70) * mm});
            skLineSegment(sketch, "E76.left", {"start": v(102, 77) * mm, "end": v(102, 73) * mm});
            skLineSegment(sketch, "E76.right", {"start": v(119, 77) * mm, "end": v(119, 73) * mm});
            skPoint(sketch, "E77.visualSharp", {"position": v(102, 80) * mm});
            skArc(sketch, "E77.filletArc", {"start": v(105, 80) * mm, "mid": v(102.88, 79.12) * mm, "end": v(102, 77) * mm});
            skPoint(sketch, "E78.visualSharp", {"position": v(102, 70) * mm});
            skArc(sketch, "E78.filletArc", {"start": v(102, 73) * mm, "mid": v(102.88, 70.88) * mm, "end": v(105, 70) * mm});
            skPoint(sketch, "E79.visualSharp", {"position": v(119, 70) * mm});
            skArc(sketch, "E79.filletArc", {"start": v(116, 70) * mm, "mid": v(118.12, 70.88) * mm, "end": v(119, 73) * mm});
            skPoint(sketch, "E80.visualSharp", {"position": v(119, 80) * mm});
            skArc(sketch, "E80.filletArc", {"start": v(119, 77) * mm, "mid": v(118.12, 79.12) * mm, "end": v(116, 80) * mm});
            skLineSegment(sketch, "E81.bottom", {"start": v(107, 127) * mm, "end": v(111, 127) * mm});
            skLineSegment(sketch, "E81.top", {"start": v(107, 144) * mm, "end": v(111, 144) * mm});
            skLineSegment(sketch, "E81.left", {"start": v(104, 130) * mm, "end": v(104, 141) * mm});
            skLineSegment(sketch, "E81.right", {"start": v(114, 130) * mm, "end": v(114, 141) * mm});
            skPoint(sketch, "E82.visualSharp", {"position": v(104, 144) * mm});
            skArc(sketch, "E82.filletArc", {"start": v(107, 144) * mm, "mid": v(104.88, 143.12) * mm, "end": v(104, 141) * mm});
            skPoint(sketch, "E83.visualSharp", {"position": v(114, 144) * mm});
            skArc(sketch, "E83.filletArc", {"start": v(114, 141) * mm, "mid": v(113.12, 143.12) * mm, "end": v(111, 144) * mm});
            skPoint(sketch, "E84.visualSharp", {"position": v(114, 127) * mm});
            skArc(sketch, "E84.filletArc", {"start": v(111, 127) * mm, "mid": v(113.12, 127.88) * mm, "end": v(114, 130) * mm});
            skPoint(sketch, "E85.visualSharp", {"position": v(104, 127) * mm});
            skArc(sketch, "E85.filletArc", {"start": v(104, 130) * mm, "mid": v(104.88, 127.88) * mm, "end": v(107, 127) * mm});
            skSolve(sketch);
        }
        {
            var Q0;
            Q0 = qSketchRegion(id + "F25", true);
            extrude(context, id + "F26", {"entities" : qUnion([Q0]), "operationType" : NewBodyOperationType.REMOVE, "oppositeDirection" : true, "depth" : 10 * mm, "offsetDistance" : 25 * mm});
        }
    });
